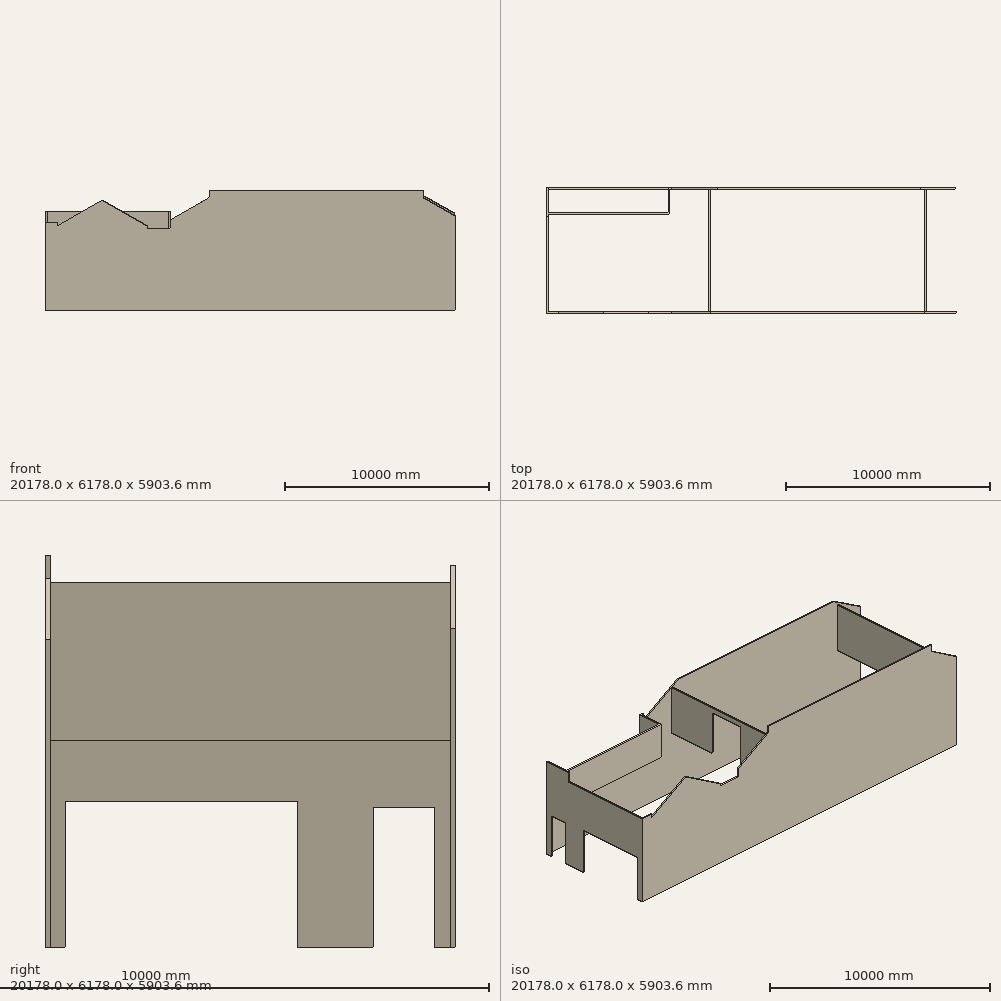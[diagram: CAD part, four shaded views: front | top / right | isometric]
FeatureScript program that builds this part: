
annotation { "Feature Type Name" : "Feature", "Feature Type Description" : "" }
export const myFeature = defineFeature(function(context is Context, id is Id, definition is map)
    precondition{}
    {
        {
            var Q0;
            Q0=qCreatedBy(makeId("Right.planeOp"),FACE);
            var sketch = newSketch(context, id + "F0", { "sketchPlane" : qUnion([Q0])});
            skLineSegment(sketch, "E0", {"start": v(0, 0) * mm, "end": v(6178, 0) * mm});
            skLineSegment(sketch, "E1", {"start": v(6178, 0) * mm, "end": v(6178, 4852) * mm});
            skLineSegment(sketch, "E2", {"start": v(4765, 4352) * mm, "end": v(0, 4352) * mm});
            skLineSegment(sketch, "E3", {"start": v(0, 4352) * mm, "end": v(0, 0) * mm});
            skLineSegment(sketch, "E4", {"start": v(4765, 4352) * mm, "end": v(4765, 4852) * mm});
            skLineSegment(sketch, "E5", {"start": v(4765, 4852) * mm, "end": v(6178, 4852) * mm});
            skLineSegment(sketch, "E6.bottom", {"start": v(5865, 0) * mm, "end": v(4945, 0) * mm});
            skLineSegment(sketch, "E6.top", {"start": v(5865, 2110) * mm, "end": v(4945, 2110) * mm});
            skLineSegment(sketch, "E6.left", {"start": v(5865, 0) * mm, "end": v(5865, 2110) * mm});
            skLineSegment(sketch, "E6.right", {"start": v(4945, 0) * mm, "end": v(4945, 2110) * mm});
            skLineSegment(sketch, "E7.bottom", {"start": v(3800, 0) * mm, "end": v(300, 0) * mm});
            skLineSegment(sketch, "E7.top", {"start": v(3800, 2200) * mm, "end": v(300, 2200) * mm});
            skLineSegment(sketch, "E7.left", {"start": v(3800, 0) * mm, "end": v(3800, 2200) * mm});
            skLineSegment(sketch, "E7.right", {"start": v(300, 0) * mm, "end": v(300, 2200) * mm});
            skSolve(sketch);
        }
        {
            var Q0;
            Q0=makeQuery(id+"F0.imprint","IMPRINT",FACE,{"disambiguationData":[TD([[makeQuery(id+"F0.imprint","IMPRINT",EDGE,{"derivedFrom":sQuery(id+"F0.wireOp",EDGE,"E0")}),1.0]])]});
            extrude(context, id + "F1", {"entities" : qUnion([Q0]), "depth" : 75 * mm});
        }
        {
            var Q0;
            Q0=makeQuery(id+"F1.opExtrude","SWEPT_FACE",FACE,{"disambiguationData":[OSD([sQuery(id+"F0.wireOp",EDGE,"E3")])]});
            var sketch = newSketch(context, id + "F2", { "sketchPlane" : qUnion([Q0])});
            skLineSegment(sketch, "E8.bottom", {"start": v(0, 0) * mm, "end": v(20178, 0) * mm});
            skLineSegment(sketch, "E8.left", {"start": v(0, 0) * mm, "end": v(0, 4352) * mm});
            skLineSegment(sketch, "E8.right", {"start": v(20178, 0) * mm, "end": v(20178, 4643.04) * mm});
            skLineSegment(sketch, "E9", {"start": v(0, 4352) * mm, "end": v(600, 4352) * mm});
            skLineSegment(sketch, "E10", {"start": v(600, 4352) * mm, "end": v(600, 4162) * mm});
            skLineSegment(sketch, "E11", {"start": v(600, 4162) * mm, "end": v(2800, 5421.95) * mm});
            skLineSegment(sketch, "E12", {"start": v(2800, 5421.95) * mm, "end": v(5000, 4162) * mm});
            skLineSegment(sketch, "E13", {"start": v(5000, 4162) * mm, "end": v(5000, 4052) * mm});
            skLineSegment(sketch, "E14", {"start": v(5000, 4052) * mm, "end": v(6175, 4052) * mm});
            skLineSegment(sketch, "E15", {"start": v(6175, 4052) * mm, "end": v(6175, 4464) * mm});
            skLineSegment(sketch, "E16", {"start": v(6175, 4464) * mm, "end": v(8077.62, 5553.64) * mm});
            skLineSegment(sketch, "E17", {"start": v(18588, 5553.64) * mm, "end": v(20178, 4643.04) * mm});
            skLineSegment(sketch, "E18", {"start": v(8077.62, 5553.64) * mm, "end": v(8077.62, 5903.64) * mm});
            skLineSegment(sketch, "E19", {"start": v(8077.62, 5903.64) * mm, "end": v(18588, 5903.64) * mm});
            skLineSegment(sketch, "E20", {"start": v(18588, 5903.64) * mm, "end": v(18588, 5553.64) * mm});
            skSolve(sketch);
        }
        {
            var Q0;
            {var subQ2=sQuery(id+"F2.wireOp",EDGE,"E8.right");Q0=makeQuery(id+"F2.imprint","IMPRINT",FACE,{"disambiguationData":[TD([[makeQuery(id+"F2.imprint","IMPRINT",EDGE,{"derivedFrom":subQ2}),1.0]])]});}
            extrude(context, id + "F3", {"entities" : qUnion([Q0]), "operationType" : NewBodyOperationType.ADD, "oppositeDirection" : true, "depth" : 75 * mm});
        }
        {
            var Q0;
            Q0=makeQuery(id+"F1.opExtrude","SWEPT_FACE",FACE,{"disambiguationData":[OSD([sQuery(id+"F0.wireOp",EDGE,"E1")])]});
            var sketch = newSketch(context, id + "F4", { "sketchPlane" : qUnion([Q0])});
            skLineSegment(sketch, "E21.right", {"start": v(-20113, 0) * mm, "end": v(-20113, 4798.3) * mm});
            skLineSegment(sketch, "E22.MirrorCS", {"start": v(-6175, 4464) * mm, "end": v(-6175, 4852) * mm});
            skLineSegment(sketch, "E23.MirrorCS", {"start": v(0, 0) * mm, "end": v(0, 4852) * mm});
            skLineSegment(sketch, "E24.MirrorCS", {"start": v(0, 0) * mm, "end": v(-20113, 0) * mm});
            skLineSegment(sketch, "E25.MirrorCS", {"start": v(-18413.87, 5752) * mm, "end": v(-20113, 4798.3) * mm});
            skLineSegment(sketch, "E26.MirrorCS", {"start": v(-6175, 4464) * mm, "end": v(-8427.62, 5752) * mm});
            skLineSegment(sketch, "E27.MirrorCS", {"start": v(-8427.62, 5752) * mm, "end": v(-18413.87, 5752) * mm});
            skPoint(sketch, "E28.orphan", {"position": v(-7740.72, 4852) * mm});
            skPoint(sketch, "E29.orphan", {"position": v(-600, 4852) * mm});
            skLineSegment(sketch, "E30", {"start": v(-6075, 4852) * mm, "end": v(-6075, 3122) * mm});
            skLineSegment(sketch, "E31", {"start": v(-6075, 3122) * mm, "end": v(-75, 3122) * mm});
            skLineSegment(sketch, "E32", {"start": v(-75, 3122) * mm, "end": v(-75, 4852) * mm});
            skLineSegment(sketch, "E33", {"start": v(-6075, 4852) * mm, "end": v(-6175, 4852) * mm});
            skSolve(sketch);
        }
        {
            var Q0;
            {var subQ4=sQuery(id+"F4.wireOp",EDGE,"E21.right");Q0=makeQuery(id+"F4.imprint","IMPRINT",FACE,{"disambiguationData":[TD([[makeQuery(id+"F4.imprint","IMPRINT",EDGE,{"derivedFrom":subQ4}),-1.0]])]});}
            extrude(context, id + "F5", {"entities" : qUnion([Q0]), "operationType" : NewBodyOperationType.ADD, "oppositeDirection" : true, "depth" : 75 * mm});
        }
        {
            var Q0;
            Q0=makeQuery(id+"F5.opExtrude","SWEPT_FACE",FACE,{"disambiguationData":[OSD([sQuery(id+"F4.wireOp",EDGE,"E30")])]});
            var sketch = newSketch(context, id + "F6", { "sketchPlane" : qUnion([Q0])});
            skLineSegment(sketch, "E34.bottom", {"start": v(-6178, 3122) * mm, "end": v(-4865, 3122) * mm});
            skLineSegment(sketch, "E34.top", {"start": v(-6178, 4852) * mm, "end": v(-4865, 4852) * mm});
            skLineSegment(sketch, "E34.left", {"start": v(-6178, 3122) * mm, "end": v(-6178, 4852) * mm});
            skLineSegment(sketch, "E34.right", {"start": v(-4865, 3122) * mm, "end": v(-4865, 4852) * mm});
            skSolve(sketch);
        }
        {
            var Q0;
            Q0 = qSketchRegion(id + "F6", true);
            extrude(context, id + "F7", {"entities" : qUnion([Q0]), "operationType" : NewBodyOperationType.ADD, "depth" : 75 * mm});
        }
        {
            var Q0;
            Q0=makeQuery(id+"F7.opExtrude","SWEPT_FACE",FACE,{"disambiguationData":[OSD([sQuery(id+"F6.wireOp",EDGE,"E34.right")])]});
            var sketch = newSketch(context, id + "F8", { "sketchPlane" : qUnion([Q0])});
            skLineSegment(sketch, "E35.bottom", {"start": v(6075, 4852) * mm, "end": v(75, 4852) * mm});
            skLineSegment(sketch, "E35.top", {"start": v(6075, 3122) * mm, "end": v(75, 3122) * mm});
            skLineSegment(sketch, "E35.left", {"start": v(6075, 4852) * mm, "end": v(6075, 3122) * mm});
            skLineSegment(sketch, "E35.right", {"start": v(75, 4852) * mm, "end": v(75, 3122) * mm});
            skSolve(sketch);
        }
        {
            var Q0;
            {var subQ2=sQuery(id+"F8.wireOp",EDGE,"E35.right");Q0=makeQuery(id+"F8.imprint","IMPRINT",FACE,{"disambiguationData":[TD([[makeQuery(id+"F8.imprint","IMPRINT",EDGE,{"derivedFrom":subQ2}),1.0]])]});}
            extrude(context, id + "F9", {"entities" : qUnion([Q0]), "operationType" : NewBodyOperationType.ADD, "oppositeDirection" : true, "depth" : 75 * mm});
        }
        {
            var Q0;
            Q0=makeQuery(id+"F3.opExtrude","CAP_FACE",FACE,{"disambiguationData":[OSD([sQuery(id+"F0.wireOp",EDGE,"E3"),sQuery(id+"F2.wireOp",EDGE,"E8.bottom"),sQuery(id+"F2.wireOp",EDGE,"E8.right"),sQuery(id+"F2.wireOp",EDGE,"E9"),sQuery(id+"F2.wireOp",EDGE,"E10"),sQuery(id+"F2.wireOp",EDGE,"E11"),sQuery(id+"F2.wireOp",EDGE,"E12"),sQuery(id+"F2.wireOp",EDGE,"E13"),sQuery(id+"F2.wireOp",EDGE,"E14"),sQuery(id+"F2.wireOp",EDGE,"E15"),sQuery(id+"F2.wireOp",EDGE,"E16"),sQuery(id+"F2.wireOp",EDGE,"E17"),sQuery(id+"F2.wireOp",EDGE,"E18"),sQuery(id+"F2.wireOp",EDGE,"E19"),sQuery(id+"F2.wireOp",EDGE,"E20")])],"isStart":false});
            var sketch = newSketch(context, id + "F10", { "sketchPlane" : qUnion([Q0])});
            skLineSegment(sketch, "E36.bottom", {"start": v(-8048, 3122) * mm, "end": v(-7973, 3122) * mm});
            skLineSegment(sketch, "E36.top", {"start": v(-8048, 5497) * mm, "end": v(-7973, 5497) * mm});
            skLineSegment(sketch, "E36.left", {"start": v(-8048, 3122) * mm, "end": v(-8048, 5497) * mm});
            skLineSegment(sketch, "E36.right", {"start": v(-7973, 3122) * mm, "end": v(-7973, 5497) * mm});
            skSolve(sketch);
        }
        {
            var Q0;
            Q0=makeQuery(id+"F10.imprint","IMPRINT",FACE,{"disambiguationData":[TD([[makeQuery(id+"F10.imprint","IMPRINT",EDGE,{"derivedFrom":sQuery(id+"F10.wireOp",EDGE,"E36.bottom")}),1.0]])]});
            var Q1;
            Q1=makeQuery(id+"F5.opExtrude","CAP_FACE",FACE,{"disambiguationData":[OSD([sQuery(id+"F0.wireOp",EDGE,"E1"),sQuery(id+"F4.wireOp",EDGE,"E21.right"),sQuery(id+"F4.wireOp",EDGE,"E22.MirrorCS"),sQuery(id+"F4.wireOp",EDGE,"E24.MirrorCS"),sQuery(id+"F4.wireOp",EDGE,"E25.MirrorCS"),sQuery(id+"F4.wireOp",EDGE,"E26.MirrorCS"),sQuery(id+"F4.wireOp",EDGE,"E27.MirrorCS"),sQuery(id+"F4.wireOp",EDGE,"E30"),sQuery(id+"F4.wireOp",EDGE,"E31"),sQuery(id+"F4.wireOp",EDGE,"E33")])],"isStart":false});
            extrude(context, id + "F11", {"entities" : qUnion([Q0]), "operationType" : NewBodyOperationType.ADD, "endBound" : BoundingType.UP_TO_SURFACE, "endBoundEntityFace" : qUnion([Q1]), "depth" : 25 * mm});
        }
        {
            var Q0;
            Q0=makeQuery(id+"F11.opExtrude","SWEPT_FACE",FACE,{"disambiguationData":[OSD([sQuery(id+"F10.wireOp",EDGE,"E36.right")])]});
            var sketch = newSketch(context, id + "F12", { "sketchPlane" : qUnion([Q0])});
            skLineSegment(sketch, "E37.bottom", {"start": v(-3497, 3122) * mm, "end": v(-1675, 3122) * mm});
            skLineSegment(sketch, "E37.top", {"start": v(-3497, 5234) * mm, "end": v(-1675, 5234) * mm});
            skLineSegment(sketch, "E37.left", {"start": v(-3497, 3122) * mm, "end": v(-3497, 5234) * mm});
            skLineSegment(sketch, "E37.right", {"start": v(-1675, 3122) * mm, "end": v(-1675, 5234) * mm});
            skSolve(sketch);
        }
        {
            var Q0;
            Q0=makeQuery(id+"F12.imprint","IMPRINT",FACE,{"disambiguationData":[TD([[makeQuery(id+"F12.imprint","IMPRINT",EDGE,{"derivedFrom":sQuery(id+"F12.wireOp",EDGE,"E37.bottom")}),1.0]])]});
            extrude(context, id + "F13", {"entities" : qUnion([Q0]), "operationType" : NewBodyOperationType.REMOVE, "endBound" : BoundingType.UP_TO_NEXT, "oppositeDirection" : true, "depth" : 25 * mm});
        }
        {
            var Q0;
            Q0=makeQuery(id+"F3.opExtrude","CAP_FACE",FACE,{"disambiguationData":[OSD([sQuery(id+"F0.wireOp",EDGE,"E3"),sQuery(id+"F2.wireOp",EDGE,"E8.bottom"),sQuery(id+"F2.wireOp",EDGE,"E8.right"),sQuery(id+"F2.wireOp",EDGE,"E9"),sQuery(id+"F2.wireOp",EDGE,"E10"),sQuery(id+"F2.wireOp",EDGE,"E11"),sQuery(id+"F2.wireOp",EDGE,"E12"),sQuery(id+"F2.wireOp",EDGE,"E13"),sQuery(id+"F2.wireOp",EDGE,"E14"),sQuery(id+"F2.wireOp",EDGE,"E15"),sQuery(id+"F2.wireOp",EDGE,"E16"),sQuery(id+"F2.wireOp",EDGE,"E17"),sQuery(id+"F2.wireOp",EDGE,"E18"),sQuery(id+"F2.wireOp",EDGE,"E19"),sQuery(id+"F2.wireOp",EDGE,"E20")])],"isStart":false});
            var sketch = newSketch(context, id + "F14", { "sketchPlane" : qUnion([Q0])});
            skLineSegment(sketch, "E38.bottom", {"start": v(-18688, 3122) * mm, "end": v(-18613, 3122) * mm});
            skLineSegment(sketch, "E38.top", {"start": v(-18688, 5497) * mm, "end": v(-18613, 5497) * mm});
            skLineSegment(sketch, "E38.left", {"start": v(-18688, 3122) * mm, "end": v(-18688, 5497) * mm});
            skLineSegment(sketch, "E38.right", {"start": v(-18613, 3122) * mm, "end": v(-18613, 5497) * mm});
            skSolve(sketch);
        }
        {
            var Q0;
            {var subQ1=sQuery(id+"F14.wireOp",EDGE,"E38.bottom");Q0=makeQuery(id+"F14.imprint","IMPRINT",FACE,{"disambiguationData":[TD([[makeQuery(id+"F14.imprint","IMPRINT",EDGE,{"derivedFrom":subQ1}),1.0]])]});}
            extrude(context, id + "F15", {"entities" : qUnion([Q0]), "operationType" : NewBodyOperationType.ADD, "endBound" : BoundingType.UP_TO_NEXT, "depth" : 25 * mm});
        }
    });
